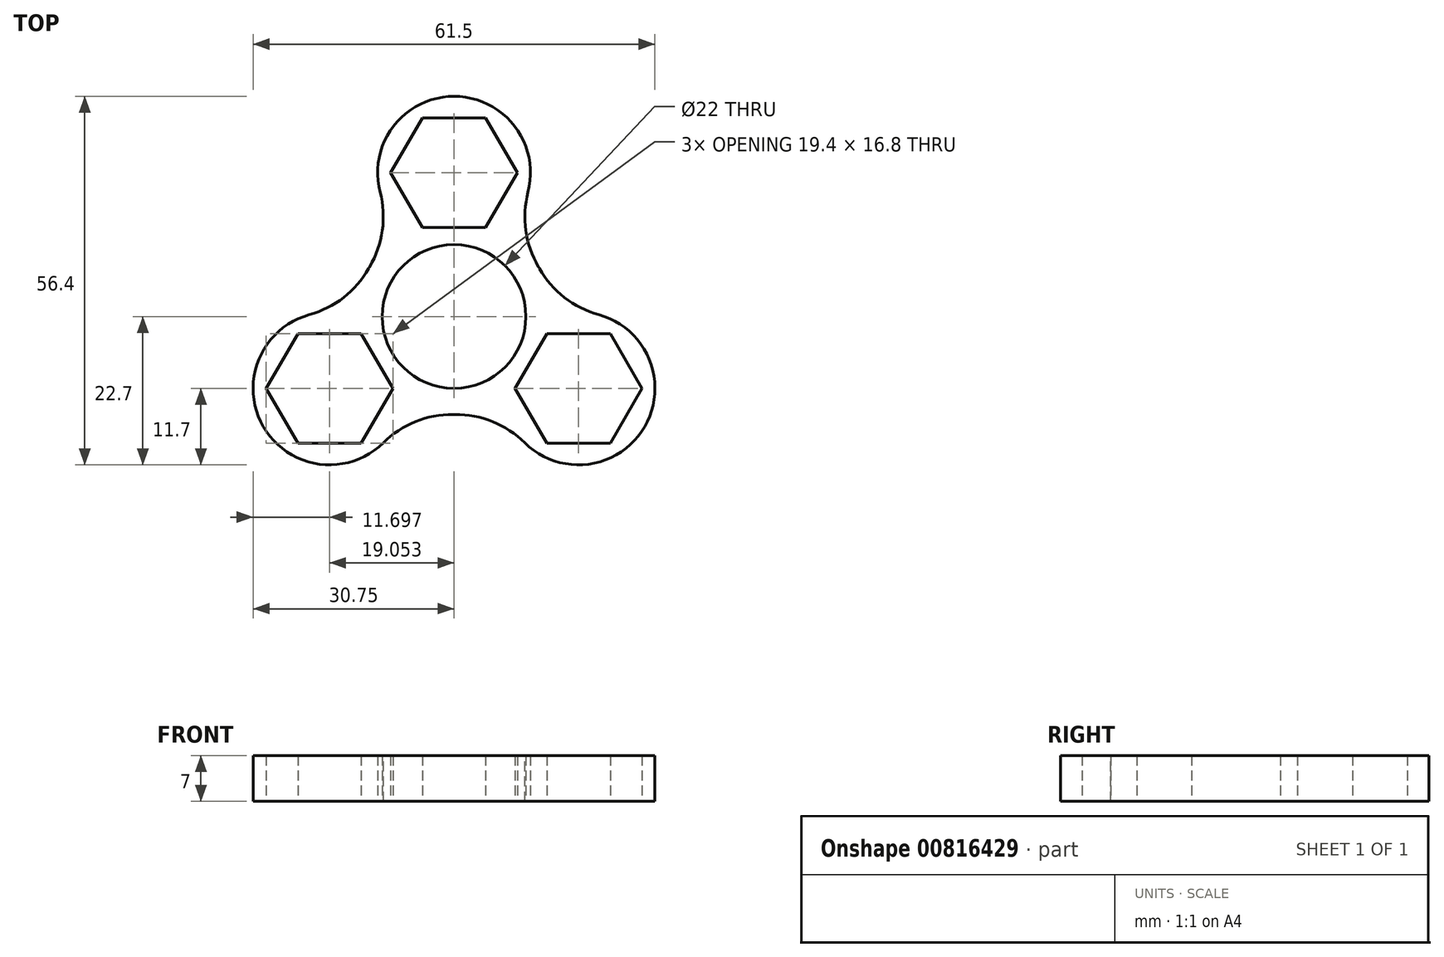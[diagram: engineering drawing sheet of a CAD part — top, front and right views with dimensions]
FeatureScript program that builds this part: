
annotation { "Feature Type Name" : "Feature", "Feature Type Description" : "" }
export const myFeature = defineFeature(function(context is Context, id is Id, definition is map)
    precondition{}
    {
        {
            var Q0;
            Q0=qCreatedBy(makeId("Top.planeOp"),FACE);
            var sketch = newSketch(context, id + "F0", { "sketchPlane" : qUnion([Q0])});
            skCircle(sketch, "E0", {"center": v(0, 0) * mm, "radius": 11 * mm});
            skCircle(sketch, "E1.0", {"center": v(0, 0) * mm, "radius": 15 * mm});
            skLineSegment(sketch, "E2", {"start": v(0, 0) * mm, "end": v(0, 22) * mm, "construction": true});
            skCircle(sketch, "E3.cCircle", {"center": v(0, 22) * mm, "radius": 8.4 * mm, "construction": true});
            skLineSegment(sketch, "E3.0", {"start": v(4.85, 13.6) * mm, "end": v(-4.85, 13.6) * mm});
            skLineSegment(sketch, "E3.1", {"start": v(-4.85, 13.6) * mm, "end": v(-9.7, 22) * mm});
            skLineSegment(sketch, "E3.2", {"start": v(-9.7, 22) * mm, "end": v(-4.85, 30.4) * mm});
            skLineSegment(sketch, "E3.3", {"start": v(-4.85, 30.4) * mm, "end": v(4.85, 30.4) * mm});
            skLineSegment(sketch, "E3.4", {"start": v(4.85, 30.4) * mm, "end": v(9.7, 22) * mm});
            skLineSegment(sketch, "E3.5", {"start": v(9.7, 22) * mm, "end": v(4.85, 13.6) * mm});
            skPoint(sketch, "E3.0.midPoint", {"position": v(0, 13.6) * mm});
            skArc(sketch, "E4", {"start": v(7.48, 13) * mm, "mid": v(0, 33.7) * mm, "end": v(-7.48, 13) * mm});
            skLineSegment(sketch, "E5", {"start": v(0, 22) * mm, "end": v(-5.85, 32.13) * mm, "construction": true});
            skArc(sketch, "E6.1.0", {"start": v(-15, -0.02) * mm, "mid": v(-29.18, -16.85) * mm, "end": v(-7.52, -12.98) * mm});
            skLineSegment(sketch, "E6.1.1", {"start": v(-14.2, -19.4) * mm, "end": v(-23.9, -19.4) * mm});
            skLineSegment(sketch, "E6.1.2", {"start": v(-9.35, -11) * mm, "end": v(-14.2, -19.4) * mm});
            skLineSegment(sketch, "E6.1.3", {"start": v(-28.75, -11) * mm, "end": v(-23.9, -2.6) * mm});
            skLineSegment(sketch, "E6.1.4", {"start": v(-23.9, -19.4) * mm, "end": v(-28.75, -11) * mm});
            skLineSegment(sketch, "E6.1.5", {"start": v(-23.9, -2.6) * mm, "end": v(-14.2, -2.6) * mm});
            skLineSegment(sketch, "E6.1.6", {"start": v(-14.2, -2.6) * mm, "end": v(-9.35, -11) * mm});
            skArc(sketch, "E6.2.0", {"start": v(7.52, -12.98) * mm, "mid": v(29.18, -16.85) * mm, "end": v(15, -0.02) * mm});
            skLineSegment(sketch, "E6.2.1", {"start": v(23.9, -2.6) * mm, "end": v(28.75, -11) * mm});
            skLineSegment(sketch, "E6.2.2", {"start": v(14.2, -2.6) * mm, "end": v(23.9, -2.6) * mm});
            skLineSegment(sketch, "E6.2.3", {"start": v(23.9, -19.4) * mm, "end": v(14.2, -19.4) * mm});
            skLineSegment(sketch, "E6.2.4", {"start": v(28.75, -11) * mm, "end": v(23.9, -19.4) * mm});
            skLineSegment(sketch, "E6.2.5", {"start": v(14.2, -19.4) * mm, "end": v(9.35, -11) * mm});
            skLineSegment(sketch, "E6.2.6", {"start": v(9.35, -11) * mm, "end": v(14.2, -2.6) * mm});
            skSolve(sketch);
        }
        {
            var Q0;
            {var subQ0=sQuery(id+"F0.wireOp",EDGE,"E6.1.0");Q0=makeQuery(id+"F0.imprint","IMPRINT",FACE,{"disambiguationData":[TD([[makeQuery(id+"F0.imprint","IMPRINT",EDGE,{"derivedFrom":subQ0}),1.0]])]});}
            var Q1;
            Q1=makeQuery(id+"F0.imprint","IMPRINT",FACE,{"disambiguationData":[TD([[makeQuery(id+"F0.imprint","IMPRINT",EDGE,{"derivedFrom":sQuery(id+"F0.wireOp",EDGE,"E0")}),-1.0]])]});
            var Q2;
            Q2=makeQuery(id+"F0.imprint","IMPRINT",FACE,{"disambiguationData":[TD([[makeQuery(id+"F0.imprint","IMPRINT",EDGE,{"derivedFrom":sQuery(id+"F0.wireOp",EDGE,"E3.0")}),1.0]])]});
            var Q3;
            {var subQ0=sQuery(id+"F0.wireOp",EDGE,"E6.2.0");Q3=makeQuery(id+"F0.imprint","IMPRINT",FACE,{"disambiguationData":[TD([[makeQuery(id+"F0.imprint","IMPRINT",EDGE,{"derivedFrom":subQ0}),1.0]])]});}
            var Q4;
            {var subQ0=sQuery(id+"F0.wireOp",EDGE,"E3.2");Q4=makeQuery(id+"F0.imprint","IMPRINT",FACE,{"disambiguationData":[TD([[makeQuery(id+"F0.imprint","IMPRINT",EDGE,{"derivedFrom":subQ0}),1.0]])]});}
            extrude(context, id + "F1", {"entities" : qUnion([Q0, Q1, Q2, Q3, Q4]), "depth" : 7 * mm, "offsetDistance" : 25 * mm});
        }
        {
            var Q0;
            {var subQ0=sQuery(id+"F0.wireOp",EDGE,"E6.2.0");var subQ1=sQuery(id+"F0.wireOp",EDGE,"E1.0");Q0=makeQuery(id+"F1.opExtrude","SWEPT_EDGE",EDGE,{"disambiguationData":[OSD([subQ1,subQ0]),TDD([makeQuery(id+"F0.imprint","INTERSECT",VERTEX,{"disambiguationData":[OD(0.0)],"derivedFrom":[subQ1,subQ0]})])]});}
            var Q1;
            {var subQ0=sQuery(id+"F0.wireOp",EDGE,"E6.1.0");var subQ1=sQuery(id+"F0.wireOp",EDGE,"E1.0");Q1=makeQuery(id+"F1.opExtrude","SWEPT_EDGE",EDGE,{"disambiguationData":[OSD([subQ1,subQ0]),TDD([makeQuery(id+"F0.imprint","INTERSECT",VERTEX,{"disambiguationData":[OD(1.0)],"derivedFrom":[subQ1,subQ0]})])]});}
            var Q2;
            {var subQ0=sQuery(id+"F0.wireOp",EDGE,"E6.1.0");var subQ1=sQuery(id+"F0.wireOp",EDGE,"E1.0");Q2=makeQuery(id+"F1.opExtrude","SWEPT_EDGE",EDGE,{"disambiguationData":[OSD([subQ1,subQ0]),TDD([makeQuery(id+"F0.imprint","INTERSECT",VERTEX,{"disambiguationData":[OD(0.0)],"derivedFrom":[subQ1,subQ0]})])]});}
            var Q3;
            {var subQ0=sQuery(id+"F0.wireOp",EDGE,"E4");var subQ1=sQuery(id+"F0.wireOp",EDGE,"E1.0");Q3=makeQuery(id+"F1.opExtrude","SWEPT_EDGE",EDGE,{"disambiguationData":[OSD([subQ1,subQ0]),TDD([makeQuery(id+"F0.imprint","INTERSECT",VERTEX,{"disambiguationData":[OD(1.0)],"derivedFrom":[subQ1,subQ0]})])]});}
            var Q4;
            {var subQ0=sQuery(id+"F0.wireOp",EDGE,"E4");var subQ1=sQuery(id+"F0.wireOp",EDGE,"E1.0");Q4=makeQuery(id+"F1.opExtrude","SWEPT_EDGE",EDGE,{"disambiguationData":[OSD([subQ1,subQ0]),TDD([makeQuery(id+"F0.imprint","INTERSECT",VERTEX,{"disambiguationData":[OD(0.0)],"derivedFrom":[subQ1,subQ0]})])]});}
            var Q5;
            {var subQ0=sQuery(id+"F0.wireOp",EDGE,"E6.2.0");var subQ1=sQuery(id+"F0.wireOp",EDGE,"E1.0");Q5=makeQuery(id+"F1.opExtrude","SWEPT_EDGE",EDGE,{"disambiguationData":[OSD([subQ1,subQ0]),TDD([makeQuery(id+"F0.imprint","INTERSECT",VERTEX,{"disambiguationData":[OD(1.0)],"derivedFrom":[subQ1,subQ0]})])]});}
            fillet(context, id + "F2", {"entities" : qUnion([Q0, Q1, Q2, Q3, Q4, Q5]), "radius" : 15 * mm, "tangentPropagation" : true, "allowEdgeOverflow" : false});
        }
    });
